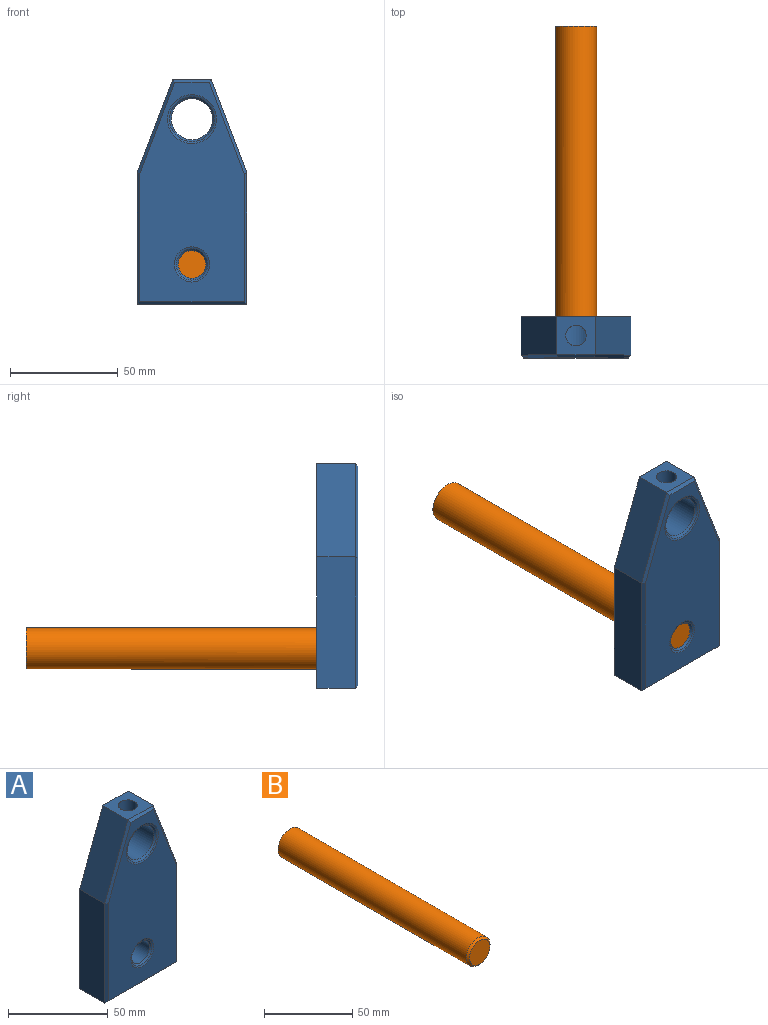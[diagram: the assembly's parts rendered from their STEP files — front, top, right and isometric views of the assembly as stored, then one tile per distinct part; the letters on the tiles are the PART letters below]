
ASSEMBLY  parts=2 mates=1
PART A: 21 faces, bbox 50.8x19x104.1 mm
  f0: plane 17.78x17.73mm, normal (0,0,1), area 244mm2, adj f1,f5,f7,f16,f20
  f1: plane 43.18x17.73mm, normal (-0.93,0,0.36), area 819.6mm2, adj f0,f2,f7,f14
  f2: plane 60.96x17.73mm, normal (-1,0,0), area 1080.8mm2, adj f1,f3,f7,f15
  f3: plane 50.8x17.73mm, normal (0,0,-1), area 900.6mm2, adj f2,f4,f7,f17
  f4: plane 60.96x17.73mm, normal (1,0,0), area 1080.8mm2, adj f3,f5,f7,f19
  f5: plane 43.18x17.73mm, normal (0.93,0,0.36), area 819.6mm2, adj f0,f4,f7,f18
  f6: plane 101.6x48.26mm, normal (0,-1,0), area 3613mm2, adj f12,f13,f14,f15,f16,f17,f18,f19
  f7: plane 104.14x50.8mm, normal (0,1,0), area 4165.7mm2, adj f0,f1,f2,f3,f4,f5,f8,f10
  f8: cylinder r=6.35mm len=17.73mm, axis (0,1,0), area 707.4mm2, adj f7,f9
  f9: cone r=7.62mm half-angle=45deg, axis (0,-1,0), area 54.3mm2, adj f8,f13
  f10: cylinder r=9.53mm len=19.05mm, axis (0,-1,0), area 987.6mm2, adj f7,f11,f20
  f11: cone r=9.53mm half-angle=45deg, axis (0,-1,0), area 79.6mm2, adj f10,f12
  f12: cone r=11.32mm half-angle=67.5deg, axis (0,-1,0), area 66.4mm2, adj f6,f11
  f13: cone r=8.15mm half-angle=67.5deg, axis (0,-1,0), area 47mm2, adj f6,f9
  f14: plane 43.41x17.38mm, normal (-0.66,-0.71,0.25), area 82mm2, adj f1,f6,f15,f16
  f15: plane 60.96x1.27mm, normal (-0.71,-0.71,0), area 108.1mm2, adj f2,f6,f14,f17
  f16: plane 17.78x1.27mm, normal (0,-0.71,0.71), area 30.4mm2, adj f0,f6,f14,f18
  f17: plane 50.8x1.27mm, normal (0,-0.71,-0.71), area 89mm2, adj f3,f6,f15,f19
  f18: plane 43.41x17.38mm, normal (0.66,-0.71,0.25), area 82mm2, adj f5,f6,f16,f19
  f19: plane 60.96x1.27mm, normal (0.71,-0.71,0), area 108.1mm2, adj f4,f6,f17,f18
  f20: cylinder r=4.76mm len=10.09mm, axis (0,0,1), area 282.3mm2, adj f0,f10
PART B: 4 faces, bbox 19.1x152.4x19.1 mm
  f0: cylinder r=9.53mm len=151.13mm, axis (0,1,0), area 9044.7mm2, adj f2,f3
  f1: plane 16.51x16.51mm, normal (0,-1,0), area 214.1mm2, adj f3
  f2: plane 19.05x19.05mm, normal (0,1,0), area 285mm2, adj f0
  f3: cone r=8.26mm half-angle=45deg, axis (0,1,0), area 100.3mm2, adj f0,f1
PLACE A t=(-37.41,-19.99,2.16)mm
PLACE B t=(-108.95,114.68,35.29)mm
MATE fastened B.f0 <-> A.f8  axis (0,-1,0) through (-76.71,-37.72,-11.34)mm
